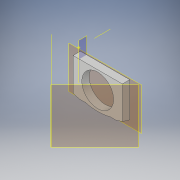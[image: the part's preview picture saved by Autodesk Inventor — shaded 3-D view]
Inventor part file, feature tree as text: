
AUTODESK INVENTOR PART (.ipt)
format: ipt  version: 2019 (Build 230136000, 136)  size: 206,336 bytes
history: native  units: in
note: dims shown in document units (in); Inventor stores cm internally (conversion verified against a paired STEP export)
features: other x8, reference x6, plane x5, sketch x4, extrude x4, projected_geometry x2, revolve x1, pattern_linear x1
ambient origin geometry x8: Origin, YZ Plane, XZ Plane, XY Plane, X Axis, Y Axis, Z Axis, Center Point
bodies: Solid1 (feature_tree)
feature tree (31):
  plane  "Work Plane1"
  sketch  "Sketch1"  dims[d0=1.5748in d1=1.063in]
  plane  "Work Plane2"
  extrude  "Extrusion1"  Depth=1.063in
  plane  "Work Plane3"
  revolve  "Revolution1"  Angle=90.0deg
  pattern_linear  "Rectangular Pattern1"  Count1=2  [1 undecoded]
  extrude  "Extrusion2"  Depth=0.3937in TaperAngle=0.0deg
  plane  "Work Plane4"
  extrude  "Extrusion3"  Depth=0.3937in TaperAngle=0.0deg
  plane  "Work Plane5"
  extrude  "Extrusion4"  Depth=0.3937in
  reference  "Reference1"
  reference  "Reference2"
  other  "Work Axis1"
  other  "Work Point1"
  sketch  "Sketch3"  dims[d3=0.3937in d4=0.0in d7=90.0deg d8=0.7874in d10=0.7874in d11=0.7874in d13=1.1811in]
  reference  "Reference3"
  reference  "Reference4"
  projected_geometry  "Projected Loop1"
  sketch  "Sketch4"  dims[d14=0.0394in d15=0.3937in d16=0.0in]
  reference  "Reference5"
  projected_geometry  "Projected Loop2"
  sketch  "Sketch5"  dims[d17=0.3937in d18=0.0in d19=0.3937in d20=0.0in d22=0.1929in d23=0.0591in d24=0.0591in d25=1.0118in]
  reference  "Reference6"
  other  "Assembly_Cube_Kinematic_Mirrormount_45_Thorlabs.iam"
  other  "20_Cube_Insert_Kinematic_Mirrormount_45_base:1"
  other  "00_PF10-03-P01-Step:1"
  other  "Assembly_Cube_empty_1x1_v2:1"
  other  "10_Cube_1x1_v2:1"
  other  "DIN 912 - replaced by DIN EN ISO 4762 M3 x 12:2"
note: 1 required parameter value undecoded (feature->parameter linkage not recoverable at this tier; creation-order binding heuristic only, values carry confidence <= 0.55)
